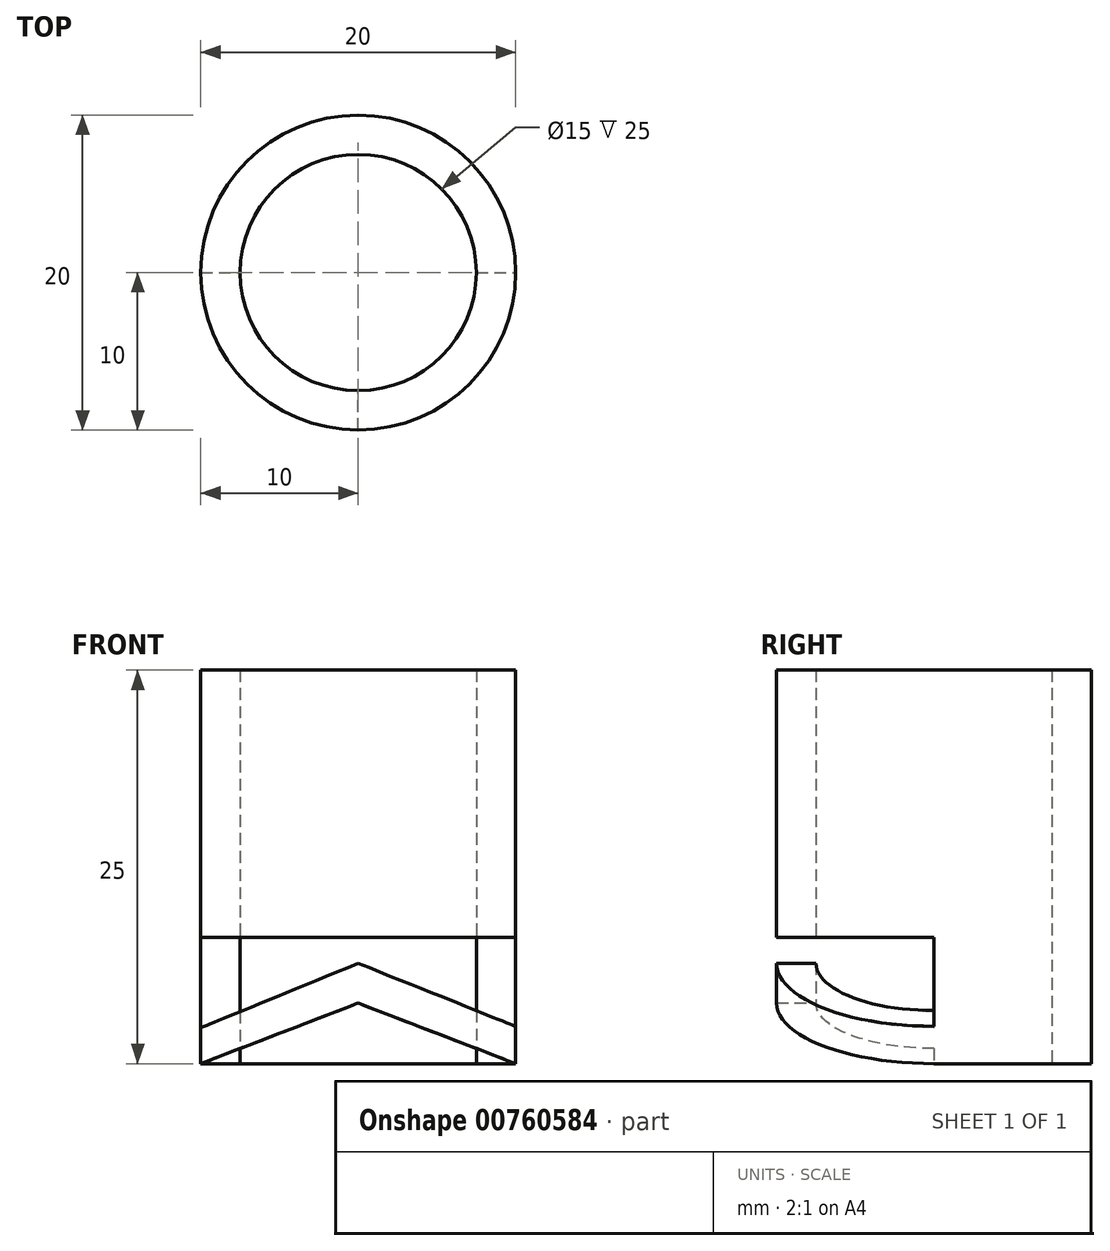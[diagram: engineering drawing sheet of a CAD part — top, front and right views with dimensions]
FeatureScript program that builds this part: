
annotation { "Feature Type Name" : "Feature", "Feature Type Description" : "" }
export const myFeature = defineFeature(function(context is Context, id is Id, definition is map)
    precondition{}
    {
        {
            var Q0;
            Q0=qCreatedBy(makeId("Top.planeOp"),FACE);
            var sketch = newSketch(context, id + "F0", { "sketchPlane" : qUnion([Q0])});
            skCircle(sketch, "E0", {"center": v(0, 0) * mm, "radius": 7.5 * mm});
            skCircle(sketch, "E1", {"center": v(0, 0) * mm, "radius": 10 * mm});
            skSolve(sketch);
        }
        {
            var Q0;
            Q0=makeQuery(id+"F0.imprint","IMPRINT",FACE,{"disambiguationData":[TD([[makeQuery(id+"F0.imprint","IMPRINT",EDGE,{"derivedFrom":sQuery(id+"F0.wireOp",EDGE,"E0")}),-1.0]])]});
            extrude(context, id + "F1", {"entities" : qUnion([Q0]), "depth" : 25 * mm, "offsetDistance" : 25 * mm});
        }
        {
            var Q0;
            Q0=qCreatedBy(makeId("Front.planeOp"),FACE);
            var sketch = newSketch(context, id + "F2", { "sketchPlane" : qUnion([Q0])});
            skLineSegment(sketch, "E2", {"start": v(-10, 0) * mm, "end": v(-10, 25) * mm});
            skLineSegment(sketch, "E3.0", {"start": v(-10, 0) * mm, "end": v(10, 0) * mm});
            skLineSegment(sketch, "E4", {"start": v(10, 25) * mm, "end": v(10, 0) * mm});
            skLineSegment(sketch, "E5", {"start": v(0, 11.16) * mm, "end": v(0, 0) * mm});
            skLineSegment(sketch, "E6", {"start": v(-10, 0) * mm, "end": v(0, 3.85) * mm});
            skLineSegment(sketch, "E7", {"start": v(0, 3.85) * mm, "end": v(10, 0) * mm});
            skLineSegment(sketch, "E8", {"start": v(-10, 0) * mm, "end": v(-10, 2.28) * mm});
            skLineSegment(sketch, "E9", {"start": v(-10, 2.28) * mm, "end": v(0, 6.37) * mm});
            skLineSegment(sketch, "E10", {"start": v(0, 6.37) * mm, "end": v(10, 2.37) * mm});
            skLineSegment(sketch, "E11", {"start": v(10, 2.37) * mm, "end": v(10, 0) * mm});
            skLineSegment(sketch, "E12", {"start": v(-10, 2.28) * mm, "end": v(-10, 8.02) * mm});
            skLineSegment(sketch, "E13", {"start": v(-10, 8.02) * mm, "end": v(10, 8.02) * mm});
            skLineSegment(sketch, "E14", {"start": v(10, 8.02) * mm, "end": v(10, 2.37) * mm});
            skSolve(sketch);
        }
        {
            var Q0;
            {var subQ3=sQuery(id+"F2.wireOp",EDGE,"E6");Q0=makeQuery(id+"F2.imprint","IMPRINT",FACE,{"disambiguationData":[TD([[makeQuery(id+"F2.imprint","IMPRINT",EDGE,{"derivedFrom":subQ3}),-1.0]])]});}
            var Q1;
            {var subQ3=sQuery(id+"F2.wireOp",EDGE,"E7");Q1=makeQuery(id+"F2.imprint","IMPRINT",FACE,{"disambiguationData":[TD([[makeQuery(id+"F2.imprint","IMPRINT",EDGE,{"derivedFrom":subQ3}),-1.0]])]});}
            var Q2;
            {var subQ0=sQuery(id+"F2.wireOp",EDGE,"E9");Q2=makeQuery(id+"F2.imprint","IMPRINT",FACE,{"disambiguationData":[TD([[makeQuery(id+"F2.imprint","IMPRINT",EDGE,{"derivedFrom":subQ0}),1.0]])]});}
            var Q3;
            {var subQ0=sQuery(id+"F2.wireOp",EDGE,"E10");Q3=makeQuery(id+"F2.imprint","IMPRINT",FACE,{"disambiguationData":[TD([[makeQuery(id+"F2.imprint","IMPRINT",EDGE,{"derivedFrom":subQ0}),1.0]])]});}
            extrude(context, id + "F3", {"entities" : qUnion([Q0, Q1, Q2, Q3]), "operationType" : NewBodyOperationType.REMOVE, "depth" : 25 * mm, "offsetDistance" : 25 * mm});
        }
    });
